# Revit family: IS_Joy_BD461_BIM_NL
name_source: partatom
category: Plumbing Fixtures
units: mm (PartAtom-declared; Revit-internal decimal feet)

## family parameters
Always vertical = No
Cut with Voids When Loaded = No
OmniClass Number = 23.45.55.17
OmniClass Title = Mixing Faucets
Part Type = Normal
Room Calculation Point = No
Round Connector Dimension = Use Diameter
Shared = No
Work Plane-Based = No

## types (4) — shared parameters
Accesoires = https://www.idealstandard.nl
Accessories = https://www.idealstandard.nl
Afmetingen = 151 x 268 x 960 mm
AfstandsEenheid = Millimeter
AssetType = Fixed
Auteur = Ideal Standard
BIMObjectName = ISI_IdealStandard_Washbasin manual water supply sets_Joy_BD461
BIMobject category = Taps & Mixers
BIMobject category code = sanitary-taps-mixers
BIMobject main category = Sanitary
BIMobject main category code = sanitary
Beschrijvinggarantie = Herstellergarantie
BimObjectNaam = ISI_IdealStandard_Washbasin manual water supply sets_Joy_BD461
Brand = Ideal Standard
Brand url = https://www.idealstandard.nl
ConnectionType = Fixed
CurrencyUnit = €
Date of publishing = 20/06/2023
Diepte = 151 mm
DistributedBy = Ideal Standard
DurationUnit = Years
Edition number = 1
ExpectedLife = 30
FaucetFunction = MIXED
FaucetOperation = OTHER
FaucetType = OTHER
Garantieonderdelen = 5
Garantieunits = Jaren
GemaaktOp = 20/06/2023
Help = https://www.idealstandard.nl
Hoogte = 960,091808551922
Hulp = https://www.idealstandard.nl
IFC Classification = Sanitary Terminal
IfcExportAs = IfcValveType
IfcExportType = FAUCET
Installatieinstructies = https://www.idealstandard.nl
Installation instructions = https://www.idealstandard.nl
InstallationInstructions = https://www.idealstandard.nl
IsBuiltIn = No
IsHighPressure = No
Lengte = 268 mm
LinearUnits = milimeter
MaintenanceInformation = https://www.idealstandard.nl
Manufacturer = Ideal Standard
Manufacturer name = Ideal Standard
ManufacturerURL = https://www.idealstandard.nl
Materiaal = Messing
Material = Brass
Material main = Brass
Merk = Ideal Standard
ModelNumber = BD461
NBS Reference Code = 35-06-82
NBS Reference Description = Shower Mixers
Name = Washbasin manual water supply sets_Joy_BD461_IdealStandard
NettWeight = 7,521
Nettogewicht = 7.521
NominalHeight = 960 mm
NominalLength = 268 mm
NominalWidth = 151 mm
OmniClass Code = 23-31 11 00
OmniClass Description = Faucets
OppervlakteEenheid = Millimeter
Product Guid = 4fedbbfd-9384-484d-8c44-b90d2e0fa593
Product SKU = BD461
Product certification = https://www.idealstandard.nl
Product data url = https://bimobject.com
Product family = JOY
Product group = Taps & Mixers
Product name = Joy Freestanding Bath & Shower Mixer Kit 2 and Shower Set
Product url = https://www.idealstandard.nl
ProductInformation = https://www.idealstandard.nl
ProductSoort = Sanitair
Productinformatie = https://www.idealstandard.nl
QR code = http://bimobject.com
Revisie = 1
Shape = Sculptured
Size = 151 x 268 x 960 mm
Space = Internal
SpareParts = https://www.idealstandard.nl
SustainabilityPerformance = https://www.idealstandard.nl
Technical description = https://www.idealstandard.nl
Telefoonnummer = 077 355 08 08
TestPressure = 10 Bar
Typeconnectie = Installation
UNSPSC Code = 301815
URL = https://www.idealstandard.nl
Uniclass 1.4 Code = L725111
Uniclass 1.4 Description = Mixer taps
Uniclass 2.0 Code = PR-35-06-82
Uniclass 2.0 Description = Shower Mixers
Uniclass 2015 Code = Pr_40_20_87_78
Uniclass 2015 Name = Shower manual water supply sets
Uniclass2015Beschrijving = Pr_40_20_87_78
Uniclass2015Code = Pr_40_20_87_78
Uniclass2015Referentie = Pr_40_20_87_78
Uniclass2015Title = Shower manual water supply sets
Uniclass2015Version = v1.1
Urlproducent = https://www.idealstandard.nl
ValutaEenheid = €
Versie = 1
Version = 1
VolumeUnits = Litres
Volumeunits = Liters
Vorm = zylindrisch
WRASURL = https://www.wras.co.uk
WarrantyDescription = Manufacturers Warranty
WarrantyDurationParts = 5
WarrantyDurationUnit = year
WarrantyGuarantorParts = https://www.idealstandard.nl
Wisselstukken = https://www.idealstandard.nl
WorkingPressure = 3bar
Youtube clip = https://www.youtube.com
zero-valued in all types: Breedte, BrutoGewicht, Cost, Default Elevation, Vervangingskosten

## per-type parameters (varying)
| type | Afwerking | Artikelnummer | Artikelomschrijving | Artikelreferentie | BarCode | Barcode | Color | Description | Features | Finish | GTIN code | Kleur | MainColor | Model | ModelReference |
| BD461A2 - Joy Freestanding Bath & Shower Mixer Kit 2 and Shower Set - Brushed Gold | Geborsteld Goud | BD461A2 | Joy Vrijstaande Bad- en Douchekraan Set 2 en Doucheset - Geborsteld Goud | Joy Vrijstaande Bad- en Douchekraan Set 2 en Doucheset - Geborsteld Goud | 3800861110811 | 3800861110811 | Brushed Gold | Joy Freestanding Bath & Shower Mixer Kit 2 and Shower Set - Brushed Gold | Freestanding Bath & Shower Mixer Kit 2 and Shower Set - Brushed Gold | Brushed Gold | 3800861110811 | Geborsteld Goud | Brushed Gold | BD461A2 | BD461A2 |
| BD461A5 - Joy Freestanding Bath & Shower Mixer Kit 2 and Shower Set - Magnetic Grey | Magnetisch grijs | BD461A5 | Joy Vrijstaande Bad- en Douchekraan Set 2 en Doucheset - Magnetisch Grijs | Joy Vrijstaande Bad- en Douchekraan Set 2 en Doucheset - Magnetisch Grijs | 3800861110927 | 3800861110927 | Magnetic grey | Joy Freestanding Bath & Shower Mixer Kit 2 and Shower Set - Magnetic Grey | Freestanding Bath & Shower Mixer Kit 2 and Shower Set - Magnetic Grey | Magnetic grey | 3800861110927 | Magnetisch grijs | Magnetic grey | BD461A5 | BD461A5 |
| BD461AA - Joy Freestanding Bath & Shower Mixer Kit 2 and Shower Set - Chrome | Chroom | BD461AA | Joy Vrijstaande Bad- en Douchekraan Set 2 en Doucheset - Chroom | Joy Vrijstaande Bad- en Douchekraan Set 2 en Doucheset - Chroom | 3800861110705 | 3800861110705 | Chrome | Joy Freestanding Bath & Shower Mixer Kit 2 and Shower Set - Chrome | Freestanding Bath & Shower Mixer Kit 2 and Shower Set - Chrome | Chrome | 3800861110705 | Chroom | Chrome | BD461AA | BD461AA |
| BD461GN - Joy Freestanding Bath & Shower Mixer Kit 2 and Shower Set - Silver Storm | Zilveren storm | BD461GN | Joy Vrijstaande Bad- en Douchekraan Set 2 en Doucheset - Zilveren Storm | Joy Vrijstaande Bad- en Douchekraan Set 2 en Doucheset - Zilveren Storm | 3800861111030 | 3800861111030 | Silver storm | Joy Freestanding Bath & Shower Mixer Kit 2 and Shower Set - Silver Storm | Freestanding Bath & Shower Mixer Kit 2 and Shower Set - Silver Storm | Silver storm | 3800861111030 | Zilveren storm | Silver storm | BD461GN | BD461GN |

note: column(s) folded — value = type name in every type: Eigenschappen, Referentie

## geometry (parser evidence)
native form markers: Blend x2, Sweep x3
no freeform markers — native parametric forms only
